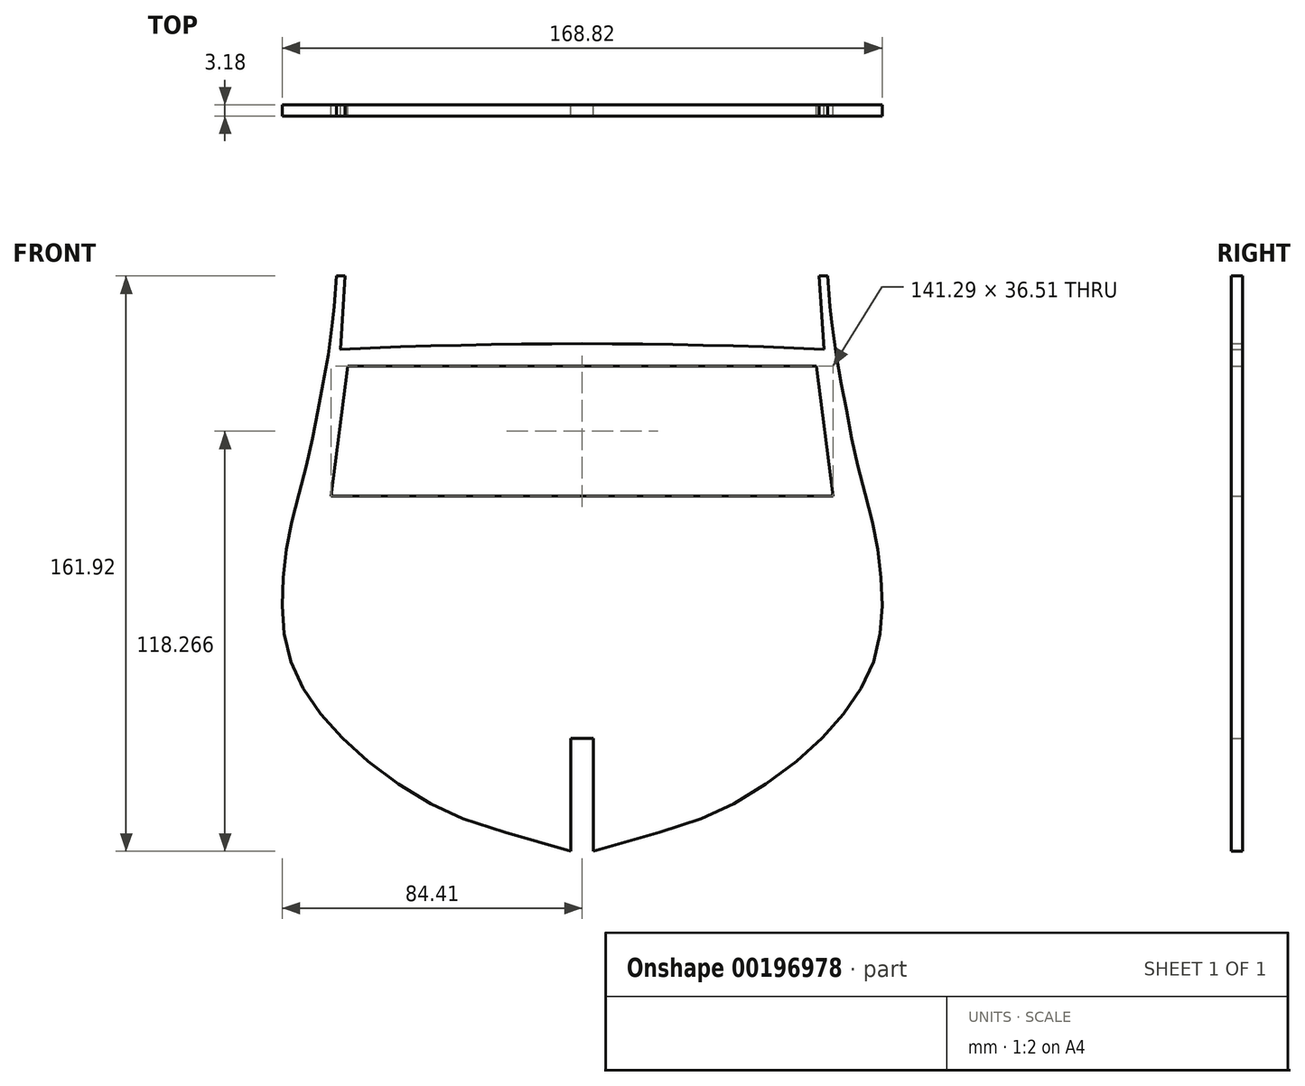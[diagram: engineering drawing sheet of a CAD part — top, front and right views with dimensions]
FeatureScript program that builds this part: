
annotation { "Feature Type Name" : "Feature", "Feature Type Description" : "" }
export const myFeature = defineFeature(function(context is Context, id is Id, definition is map)
    precondition{}
    {
        {
            var Q0;
            Q0=qCreatedBy(makeId("Front.planeOp"),FACE);
            var sketch = newSketch(context, id + "F0", { "sketchPlane" : qUnion([Q0])});
            skLineSegment(sketch, "E0", {"start": v(0, 0) * mm, "end": v(0, 36.51) * mm, "construction": true});
            skLineSegment(sketch, "E1", {"start": v(0, 36.51) * mm, "end": v(0, 42.86) * mm, "construction": true});
            skLineSegment(sketch, "E2", {"start": v(0, 0) * mm, "end": v(0, -100.01) * mm, "construction": true});
            skLineSegment(sketch, "E3", {"start": v(0, -100.01) * mm, "end": v(3.18, -100.01) * mm, "construction": true});
            skLineSegment(sketch, "E4", {"start": v(3.18, -100.01) * mm, "end": v(3.18, -68.26) * mm});
            skLineSegment(sketch, "E5", {"start": v(3.17, -68.26) * mm, "end": v(0, -68.26) * mm});
            skLineSegment(sketch, "E6", {"start": v(0, -68.26) * mm, "end": v(-3.18, -68.26) * mm});
            skLineSegment(sketch, "E7", {"start": v(-3.18, -68.26) * mm, "end": v(-3.18, -100.01) * mm});
            skLineSegment(sketch, "E8", {"start": v(-3.18, -100.01) * mm, "end": v(0, -100.01) * mm, "construction": true});
            skLineSegment(sketch, "E9", {"start": v(0, 0) * mm, "end": v(70.64, 0) * mm});
            skLineSegment(sketch, "E10", {"start": v(70.64, 0) * mm, "end": v(65.88, 36.51) * mm});
            skLineSegment(sketch, "E11", {"start": v(65.88, 36.51) * mm, "end": v(0, 36.51) * mm});
            skLineSegment(sketch, "E12", {"start": v(-65.88, 36.51) * mm, "end": v(-70.64, 0) * mm});
            skLineSegment(sketch, "E13", {"start": v(-70.64, 0) * mm, "end": v(0, 0) * mm});
            skLineSegment(sketch, "E14", {"start": v(-65.88, 36.51) * mm, "end": v(0, 36.51) * mm});
            skFitSpline(sketch, "E15", {"points": [v(3.18, -100.01) * mm, v(41.28, -87.31) * mm, v(60.33, -74.61) * mm, v(73.03, -61.91) * mm, v(80.96, -49.21) * mm, v(84.14, -36.51) * mm, v(84.14, -23.81) * mm, v(82.55, -11.11) * mm, v(79.38, 1.59) * mm, v(76.2, 14.29) * mm, v(73.82, 26.99) * mm, v(71.44, 39.69) * mm, v(69.85, 52.39) * mm, v(69.06, 61.91) * mm], "startDerivative": vector(537.46, 153.56) * mm, "endDerivative": vector(-39.38, 472.58) * mm});
            skLineSegment(sketch, "E16", {"start": v(69.06, 61.91) * mm, "end": v(66.68, 61.91) * mm});
            skLineSegment(sketch, "E17", {"start": v(66.67, 61.91) * mm, "end": v(68.03, 41.27) * mm});
            skLineSegment(sketch, "E18", {"start": v(68.03, 41.27) * mm, "end": v(71.2, 41.27) * mm, "construction": true});
            skArc(sketch, "E19", {"start": v(68.03, 41.27) * mm, "mid": v(0, 42.86) * mm, "end": v(-68.03, 41.27) * mm});
            skFitSpline(sketch, "E20.MirrorCS", {"points": [v(-3.18, -100.01) * mm, v(-41.28, -87.31) * mm, v(-60.33, -74.61) * mm, v(-73.03, -61.91) * mm, v(-80.96, -49.21) * mm, v(-84.14, -36.51) * mm, v(-84.14, -23.81) * mm, v(-82.55, -11.11) * mm, v(-79.38, 1.59) * mm, v(-76.2, 14.29) * mm, v(-73.82, 26.99) * mm, v(-71.44, 39.69) * mm, v(-69.85, 52.39) * mm, v(-69.06, 61.91) * mm], "startDerivative": vector(-537.46, 153.56) * mm, "endDerivative": vector(39.38, 472.58) * mm});
            skLineSegment(sketch, "E21.MirrorCS", {"start": v(-66.67, 61.91) * mm, "end": v(-68.03, 41.27) * mm});
            skLineSegment(sketch, "E22.MirrorCS", {"start": v(-69.06, 61.91) * mm, "end": v(-66.68, 61.91) * mm});
            skSolve(sketch);
        }
        {
            var Q0;
            Q0=makeQuery(id+"F0.imprint","IMPRINT",FACE,{"disambiguationData":[TD([[makeQuery(id+"F0.imprint","IMPRINT",EDGE,{"derivedFrom":sQuery(id+"F0.wireOp",EDGE,"E4")}),-1.0]])]});
            extrude(context, id + "F1", {"entities" : qUnion([Q0]), "endBound" : BoundingType.SYMMETRIC, "depth" : 3.17 * mm});
        }
    });
